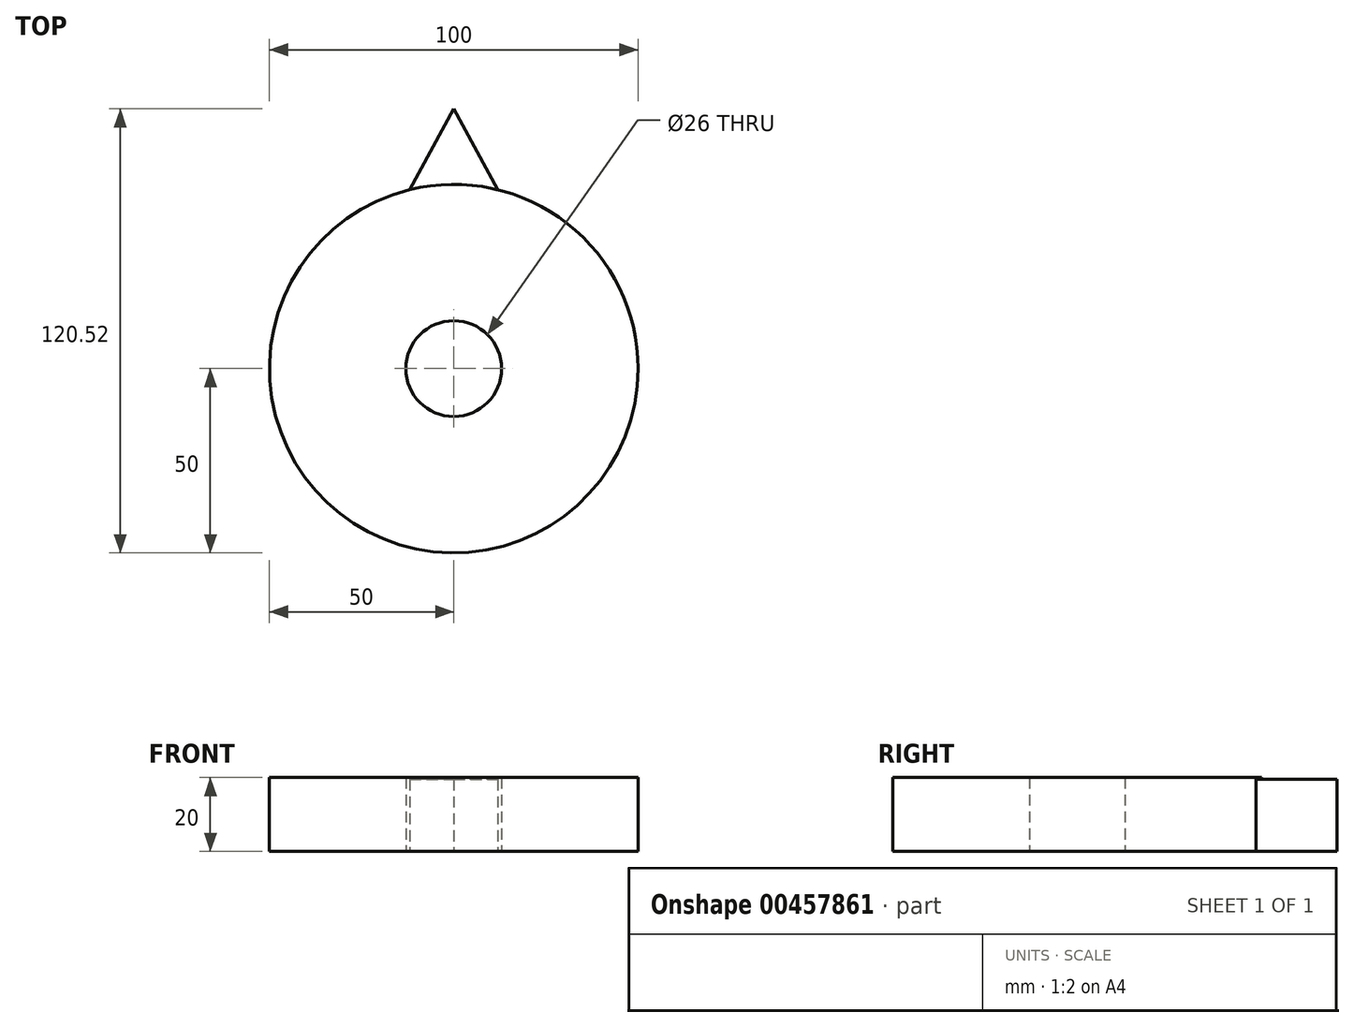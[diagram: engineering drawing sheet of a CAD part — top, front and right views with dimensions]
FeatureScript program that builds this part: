
annotation { "Feature Type Name" : "Feature", "Feature Type Description" : "" }
export const myFeature = defineFeature(function(context is Context, id is Id, definition is map)
    precondition{}
    {
        {
            var Q0;
            Q0=qCreatedBy(makeId("Top.planeOp"),FACE);
            var sketch = newSketch(context, id + "F0", { "sketchPlane" : qUnion([Q0])});
            skCircle(sketch, "E0", {"center": v(0, 0) * mm, "radius": 50 * mm});
            skSolve(sketch);
        }
        {
            var Q0;
            Q0 = qSketchRegion(id + "F0", true);
            extrude(context, id + "F1", {"entities" : qUnion([Q0]), "depth" : 20 * mm});
        }
        {
            var Q0;
            Q0=qCreatedBy(makeId("Top.planeOp"),FACE);
            var sketch = newSketch(context, id + "F2", { "sketchPlane" : qUnion([Q0])});
            skCircle(sketch, "E1", {"center": v(0, 0) * mm, "radius": 13 * mm});
            skSolve(sketch);
        }
        {
            var Q0;
            Q0 = qSketchRegion(id + "F2", true);
            extrude(context, id + "F3", {"entities" : qUnion([Q0]), "operationType" : NewBodyOperationType.REMOVE, "depth" : 20 * mm});
        }
        {
            var Q0;
            Q0=qCreatedBy(makeId("Top.planeOp"),FACE);
            var sketch = newSketch(context, id + "F4", { "sketchPlane" : qUnion([Q0])});
            skLineSegment(sketch, "E2", {"start": v(-11.93, 48.56) * mm, "end": v(0, 70.52) * mm});
            skLineSegment(sketch, "E3", {"start": v(0, 70.52) * mm, "end": v(11.93, 48.56) * mm});
            skLineSegment(sketch, "E4", {"start": v(0, 0) * mm, "end": v(0, 70.52) * mm, "construction": true});
            skArc(sketch, "E5.2", {"start": v(11.93, 48.56) * mm, "mid": v(0, 50) * mm, "end": v(-11.93, 48.56) * mm});
            skSolve(sketch);
        }
        {
            var Q0;
            Q0=makeQuery(id+"F4.imprint","IMPRINT",FACE,{"disambiguationData":[TD([[makeQuery(id+"F4.imprint","IMPRINT",EDGE,{"derivedFrom":sQuery(id+"F4.wireOp",EDGE,"E2")}),-1.0]])]});
            extrude(context, id + "F5", {"entities" : qUnion([Q0]), "operationType" : NewBodyOperationType.ADD, "depth" : 19.5 * mm});
        }
    });
